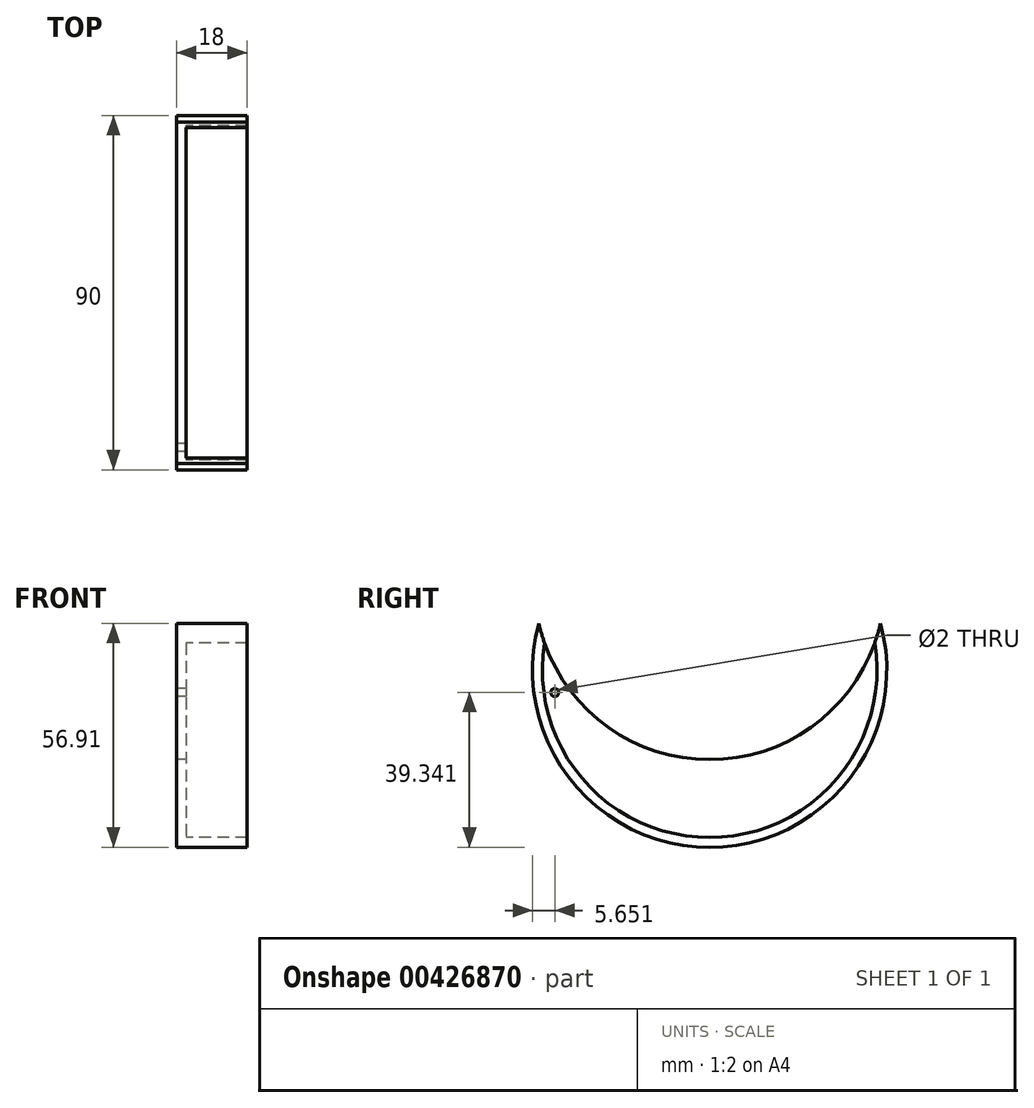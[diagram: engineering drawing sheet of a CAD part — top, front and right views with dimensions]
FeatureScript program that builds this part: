
annotation { "Feature Type Name" : "Feature", "Feature Type Description" : "" }
export const myFeature = defineFeature(function(context is Context, id is Id, definition is map)
    precondition{}
    {
        {
            var Q0;
            Q0=qCreatedBy(makeId("Front.planeOp"),FACE);
            var sketch = newSketch(context, id + "F0", { "sketchPlane" : qUnion([Q0])});
            skLineSegment(sketch, "E0.bottom", {"start": v(0, 0) * mm, "end": v(18, 0) * mm});
            skLineSegment(sketch, "E0.top", {"start": v(0, 45) * mm, "end": v(18, 45) * mm});
            skLineSegment(sketch, "E0.left", {"start": v(0, 0) * mm, "end": v(0, 45) * mm});
            skLineSegment(sketch, "E0.right", {"start": v(18, 0) * mm, "end": v(18, 45) * mm});
            skSolve(sketch);
        }
        {
            var Q0;
            Q0=makeQuery(id+"F0.imprint","IMPRINT",FACE,{"disambiguationData":[TD([[makeQuery(id+"F0.imprint","IMPRINT",EDGE,{"derivedFrom":sQuery(id+"F0.wireOp",EDGE,"E0.bottom")}),1.0]])]});
            var Q1;
            Q1=sQuery(id+"F0.wireOp",EDGE,"E0.bottom");
            revolve(context, id + "F1", {"entities" : qUnion([Q0]), "axis" : qUnion([Q1]), "revolveType" : RevolveType.FULL});
        }
        {
            var Q0;
            Q0=qCreatedBy(makeId("Right.planeOp"),FACE);
            var sketch = newSketch(context, id + "F2", { "sketchPlane" : qUnion([Q0])});
            skPoint(sketch, "E1", {"position": v(0, 0) * mm});
            skSolve(sketch);
        }
        {
            var Q0;
            Q0=sQuery(id+"F2.wireOp",VERTEX,"E1");
            var Q1;
            Q1=makeQuery(id+"F1.opRevolve","SWEPT_BODY",BODY,{"disambiguationData":[OSD([sQuery(id+"F0.wireOp",EDGE,"E0.bottom"),sQuery(id+"F0.wireOp",EDGE,"E0.top"),sQuery(id+"F0.wireOp",EDGE,"E0.left"),sQuery(id+"F0.wireOp",EDGE,"E0.right")])]});
            hole(context, id + "F3", {"style" : HoleStyle.SIMPLE, "endStyle" : HoleEndStyle.THROUGH, "oppositeDirection" : true, "holeDiameter" : 6 * mm, "isTappedThrough" : true, "tappedDepth" : 12 * mm, "tapClearance" : 3, "locations" : qUnion([Q0]), "scope" : qUnion([Q1])});
        }
        {
            var Q0;
            Q0=qCreatedBy(makeId("Right.planeOp"),FACE);
            var sketch = newSketch(context, id + "F4", { "sketchPlane" : qUnion([Q0])});
            skCircle(sketch, "E2", {"center": v(0, 21.77) * mm, "radius": 5.5 * mm});
            skSolve(sketch);
        }
        {
            var Q0;
            Q0=makeQuery(id+"F1.opRevolve","SWEPT_FACE",FACE,{"disambiguationData":[OSD([sQuery(id+"F0.wireOp",EDGE,"E0.right")])]});
            shell(context, id + "F5", {"entities" : qUnion([Q0]), "thickness" : 2.5 * mm});
        }
        {
            var Q0;
            Q0=sQuery(id+"F4.wireOp",VERTEX,"E2.center");
            var Q1;
            Q1=makeQuery(id+"F1.opRevolve","SWEPT_BODY",BODY,{"disambiguationData":[OSD([sQuery(id+"F0.wireOp",EDGE,"E0.bottom"),sQuery(id+"F0.wireOp",EDGE,"E0.top"),sQuery(id+"F0.wireOp",EDGE,"E0.left"),sQuery(id+"F0.wireOp",EDGE,"E0.right")])]});
            hole(context, id + "F6", {"style" : HoleStyle.SIMPLE, "endStyle" : HoleEndStyle.THROUGH, "oppositeDirection" : true, "holeDiameter" : 89 * mm, "isTappedThrough" : true, "tappedDepth" : 12 * mm, "tapClearance" : 3, "locations" : qUnion([Q0]), "scope" : qUnion([Q1])});
        }
        {
            var Q0;
            Q0=qCreatedBy(makeId("Right.planeOp"),FACE);
            var sketch = newSketch(context, id + "F7", { "sketchPlane" : qUnion([Q0])});
            skPoint(sketch, "E3", {"position": v(-39.35, -5.66) * mm});
            skSolve(sketch);
        }
        {
            var Q0;
            Q0=sQuery(id+"F7.wireOp",VERTEX,"E3");
            var Q1;
            Q1=makeQuery(id+"F1.opRevolve","SWEPT_BODY",BODY,{"disambiguationData":[OSD([sQuery(id+"F0.wireOp",EDGE,"E0.bottom"),sQuery(id+"F0.wireOp",EDGE,"E0.top"),sQuery(id+"F0.wireOp",EDGE,"E0.left"),sQuery(id+"F0.wireOp",EDGE,"E0.right")])]});
            hole(context, id + "F8", {"style" : HoleStyle.SIMPLE, "endStyle" : HoleEndStyle.THROUGH, "oppositeDirection" : true, "holeDiameter" : 2 * mm, "isTappedThrough" : true, "tappedDepth" : 12 * mm, "tapClearance" : 3, "locations" : qUnion([Q0]), "scope" : qUnion([Q1])});
        }
    });
